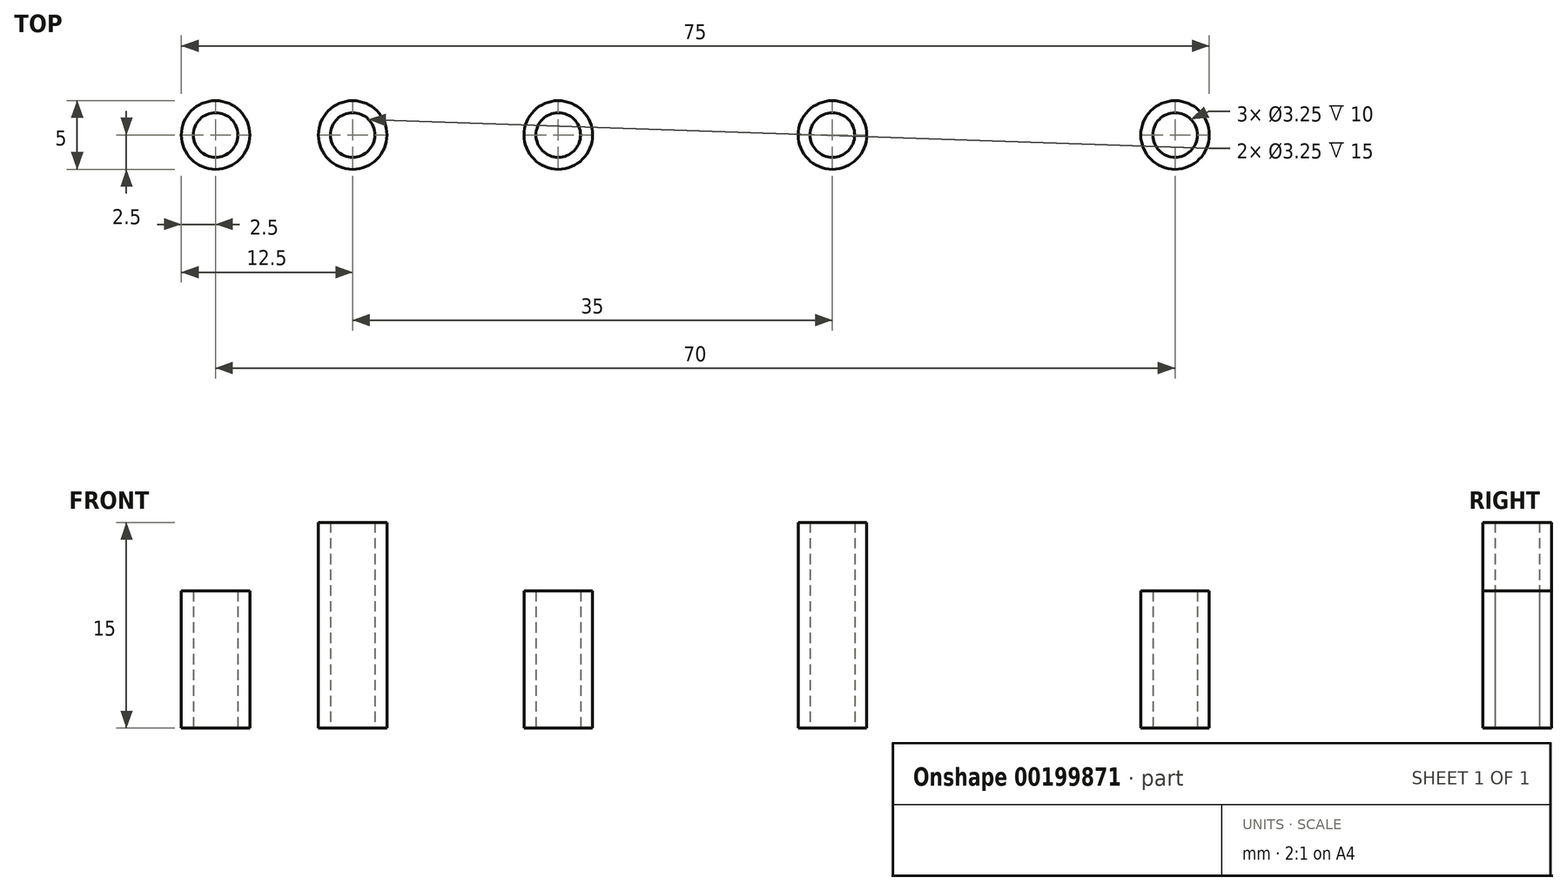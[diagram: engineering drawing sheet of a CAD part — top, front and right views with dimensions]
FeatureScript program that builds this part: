
annotation { "Feature Type Name" : "Feature", "Feature Type Description" : "" }
export const myFeature = defineFeature(function(context is Context, id is Id, definition is map)
    precondition{}
    {
        {
            var Q0;
            Q0=qCreatedBy(makeId("Top.planeOp"),FACE);
            var sketch = newSketch(context, id + "F0", { "sketchPlane" : qUnion([Q0])});
            skCircle(sketch, "E0", {"center": v(0, 0) * mm, "radius": 2.5 * mm});
            skCircle(sketch, "E1", {"center": v(0, 0) * mm, "radius": 1.63 * mm});
            skCircle(sketch, "E2.1.0.0", {"center": v(10, 0) * mm, "radius": 1.63 * mm});
            skCircle(sketch, "E2.1.0.1", {"center": v(10, 0) * mm, "radius": 2.5 * mm});
            skLineSegment(sketch, "E2.direction1", {"start": v(0, 0) * mm, "end": v(10, 0) * mm, "construction": true});
            skLineSegment(sketch, "E3.1.0.0", {"start": v(15, 0) * mm, "end": v(25, 0) * mm, "construction": true});
            skCircle(sketch, "E3.1.0.1", {"center": v(25, 0) * mm, "radius": 2.5 * mm});
            skCircle(sketch, "E3.1.0.2", {"center": v(25, 0) * mm, "radius": 1.63 * mm});
            skLineSegment(sketch, "E3.direction1", {"start": v(0, 0) * mm, "end": v(15, 0) * mm, "construction": true});
            skLineSegment(sketch, "E4.1.0.2", {"start": v(25, 0) * mm, "end": v(40, 0) * mm, "construction": true});
            skLineSegment(sketch, "E4.1.0.3", {"start": v(25, 0) * mm, "end": v(35, 0) * mm, "construction": true});
            skLineSegment(sketch, "E4.direction1", {"start": v(0, 0) * mm, "end": v(25, 0) * mm, "construction": true});
            skLineSegment(sketch, "E5.1.0.0", {"start": v(45, 0) * mm, "end": v(70, 0) * mm, "construction": true});
            skCircle(sketch, "E5.1.0.1", {"center": v(45, 0) * mm, "radius": 1.63 * mm});
            skCircle(sketch, "E5.1.0.2", {"center": v(45, 0) * mm, "radius": 2.5 * mm});
            skLineSegment(sketch, "E5.1.0.3", {"start": v(45, 0) * mm, "end": v(60, 0) * mm, "construction": true});
            skLineSegment(sketch, "E5.1.0.4", {"start": v(45, 0) * mm, "end": v(55, 0) * mm, "construction": true});
            skLineSegment(sketch, "E5.direction1", {"start": v(0, 0) * mm, "end": v(45, 0) * mm, "construction": true});
            skCircle(sketch, "E6.1.0.0", {"center": v(70, 0) * mm, "radius": 2.5 * mm});
            skLineSegment(sketch, "E6.1.0.1", {"start": v(70, 0) * mm, "end": v(85, 0) * mm, "construction": true});
            skCircle(sketch, "E6.1.0.2", {"center": v(70, 0) * mm, "radius": 1.63 * mm});
            skLineSegment(sketch, "E6.1.0.3", {"start": v(70, 0) * mm, "end": v(80, 0) * mm, "construction": true});
            skLineSegment(sketch, "E6.1.0.4", {"start": v(70, 0) * mm, "end": v(95, 0) * mm, "construction": true});
            skLineSegment(sketch, "E6.1.0.5", {"start": v(70, 0) * mm, "end": v(115, 0) * mm, "construction": true});
            skLineSegment(sketch, "E6.direction1", {"start": v(0, 0) * mm, "end": v(70, 0) * mm, "construction": true});
            skSolve(sketch);
        }
        {
            var Q0;
            Q0=makeQuery(id+"F0.imprint","IMPRINT",FACE,{"disambiguationData":[TD([[makeQuery(id+"F0.imprint","IMPRINT",EDGE,{"derivedFrom":sQuery(id+"F0.wireOp",EDGE,"E0")}),1.0]])]});
            var Q1;
            Q1=makeQuery(id+"F0.imprint","IMPRINT",FACE,{"disambiguationData":[TD([[makeQuery(id+"F0.imprint","IMPRINT",EDGE,{"derivedFrom":sQuery(id+"F0.wireOp",EDGE,"E3.1.0.2")}),-1.0]])]});
            var Q2;
            Q2=makeQuery(id+"F0.imprint","IMPRINT",FACE,{"disambiguationData":[TD([[makeQuery(id+"F0.imprint","IMPRINT",EDGE,{"derivedFrom":sQuery(id+"F0.wireOp",EDGE,"E6.1.0.0")}),1.0]])]});
            extrude(context, id + "F1", {"entities" : qUnion([Q0, Q1, Q2]), "depth" : 10 * mm});
        }
        {
            var Q0;
            Q0=makeQuery(id+"F0.imprint","IMPRINT",FACE,{"disambiguationData":[TD([[makeQuery(id+"F0.imprint","IMPRINT",EDGE,{"derivedFrom":sQuery(id+"F0.wireOp",EDGE,"E2.1.0.0")}),-1.0]])]});
            var Q1;
            Q1=makeQuery(id+"F0.imprint","IMPRINT",FACE,{"disambiguationData":[TD([[makeQuery(id+"F0.imprint","IMPRINT",EDGE,{"derivedFrom":sQuery(id+"F0.wireOp",EDGE,"E5.1.0.1")}),-1.0]])]});
            extrude(context, id + "F2", {"entities" : qUnion([Q0, Q1]), "depth" : 15 * mm});
        }
    });
